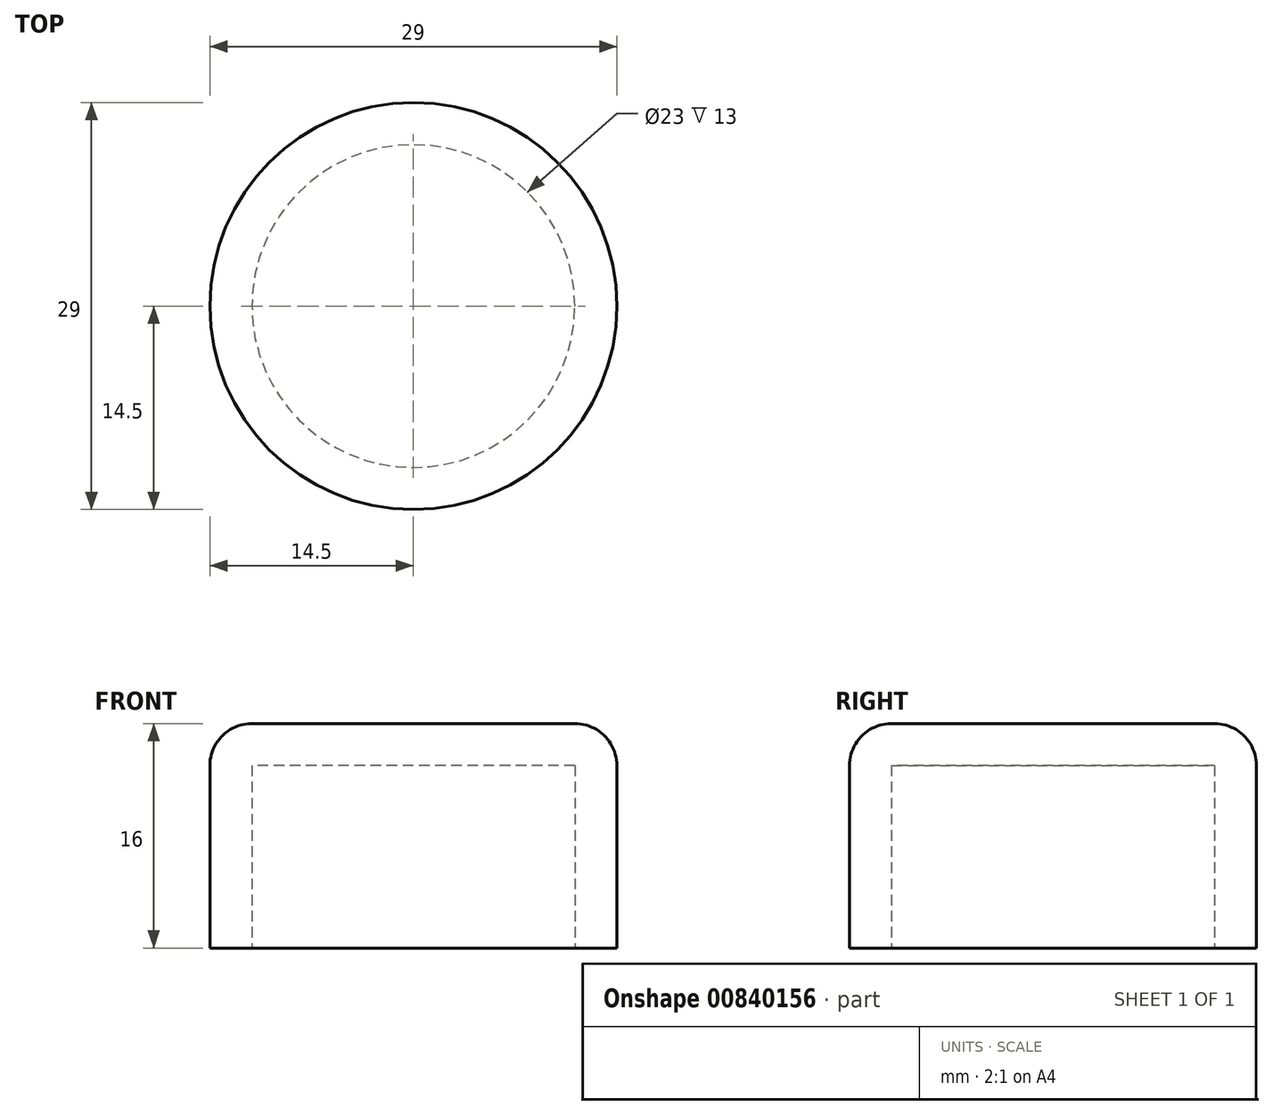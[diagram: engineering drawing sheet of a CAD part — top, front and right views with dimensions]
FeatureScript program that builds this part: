
annotation { "Feature Type Name" : "Feature", "Feature Type Description" : "" }
export const myFeature = defineFeature(function(context is Context, id is Id, definition is map)
    precondition{}
    {
        {
            var Q0;
            Q0=qCreatedBy(makeId("Top.planeOp"),FACE);
            var sketch = newSketch(context, id + "F0", { "sketchPlane" : qUnion([Q0])});
            skCircle(sketch, "E0", {"center": v(0, 0) * mm, "radius": 11.5 * mm});
            skCircle(sketch, "E1.0", {"center": v(0, 0) * mm, "radius": 14.5 * mm});
            skSolve(sketch);
        }
        {
            var Q0;
            Q0 = qSketchRegion(id + "F0", true);
            var Q1;
            Q1=makeQuery(id+"F0.imprint","IMPRINT",FACE,{"disambiguationData":[TD([[makeQuery(id+"F0.imprint","IMPRINT",EDGE,{"derivedFrom":sQuery(id+"F0.wireOp",EDGE,"E0")}),-1.0]])]});
            extrude(context, id + "F1", {"entities" : qUnion([Q0, Q1]), "depth" : 13 * mm, "offsetDistance" : 25.4 * mm});
        }
        {
            var Q0;
            Q0=makeQuery(id+"F1.opExtrude","CAP_FACE",FACE,{"disambiguationData":[OSD([sQuery(id+"F0.wireOp",EDGE,"E0"),sQuery(id+"F0.wireOp",EDGE,"E1.0")])],"isStart":false});
            var sketch = newSketch(context, id + "F2", { "sketchPlane" : qUnion([Q0])});
            skCircle(sketch, "E2.0", {"center": v(0, 0) * mm, "radius": 14.5 * mm});
            skSolve(sketch);
        }
        {
            var Q0;
            Q0=makeQuery(id+"F2.imprint","IMPRINT",FACE,{"disambiguationData":[TD([[makeQuery(id+"F2.imprint","IMPRINT",EDGE,{"derivedFrom":sQuery(id+"F2.wireOp",EDGE,"E2.0")}),1.0]])]});
            var Q1;
            Q1=makeQuery(id+"F2.imprint","IMPRINT",FACE,{"disambiguationData":[TD([[makeQuery(id+"F2.imprint","IMPRINT",EDGE,{"derivedFrom":makeQuery(id+"F1.opExtrude","CAP_EDGE",EDGE,{"disambiguationData":[OSD([sQuery(id+"F0.wireOp",EDGE,"E0")])],"isStart":false})}),1.0]])]});
            extrude(context, id + "F3", {"entities" : qUnion([Q0, Q1]), "operationType" : NewBodyOperationType.ADD, "depth" : 3 * mm, "offsetDistance" : 25 * mm});
        }
        {
            var Q0;
            Q0=makeQuery(id+"F3.opExtrude","CAP_FACE",FACE,{"disambiguationData":[OSD([sQuery(id+"F2.wireOp",EDGE,"E2.0")])],"isStart":false});
            fillet(context, id + "F4", {"entities" : qUnion([Q0]), "radius" : 3 * mm, "tangentPropagation" : true, "allowEdgeOverflow" : false});
        }
    });
